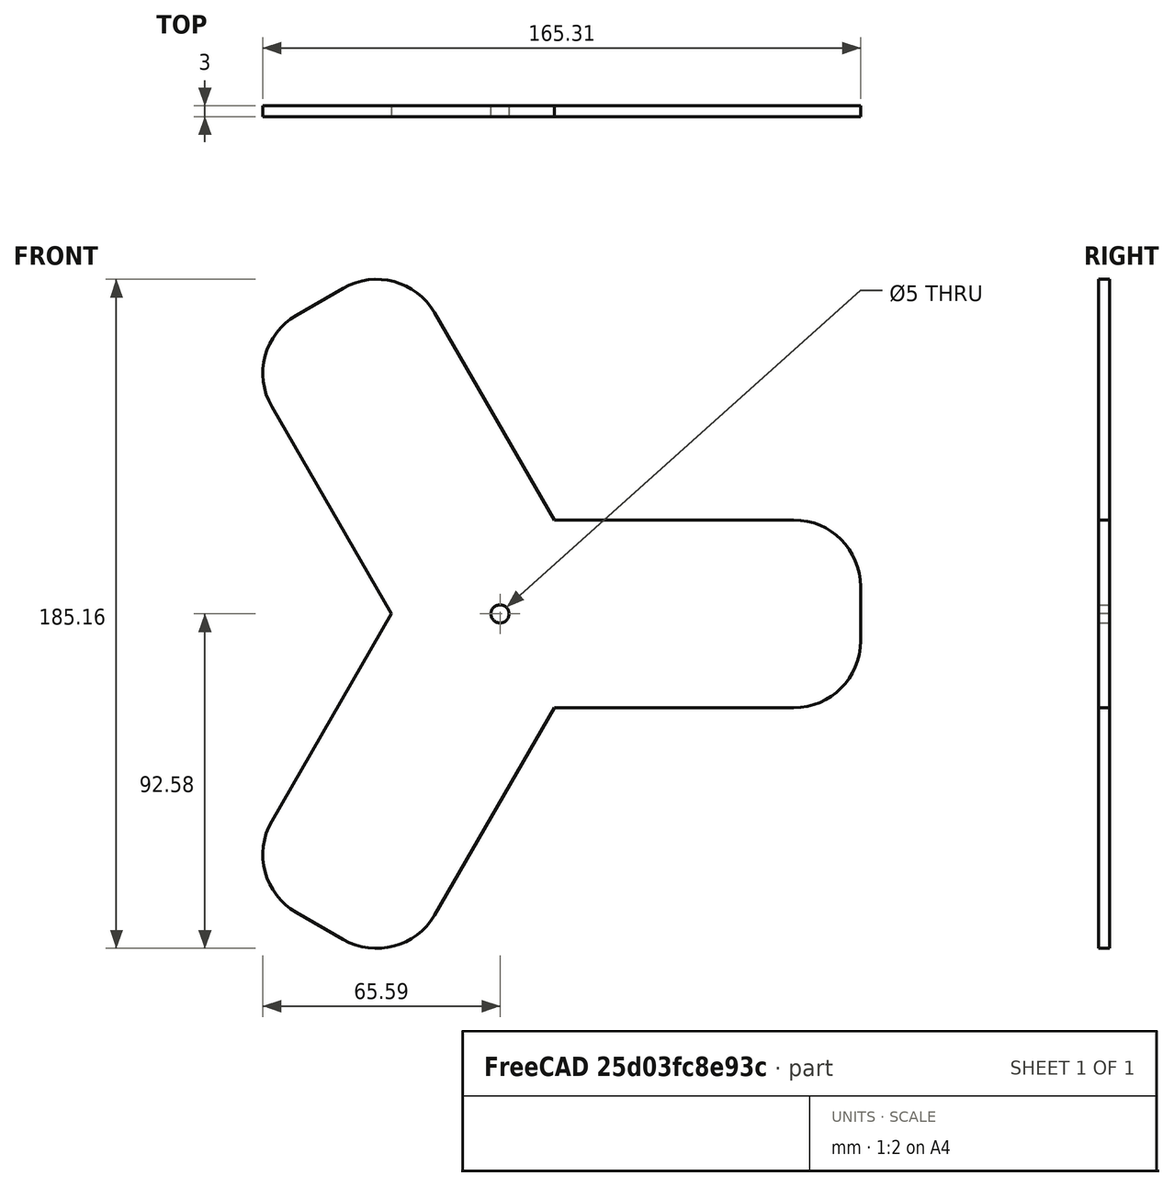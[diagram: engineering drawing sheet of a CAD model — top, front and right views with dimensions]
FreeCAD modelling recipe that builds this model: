
FCSTD DOCUMENT  (FreeCAD 0.21R33771 (Git))
Label: rotor
License: Public Domain
LicenseURL: https://en.wikipedia.org/wiki/Public_domain
objects: PartDesign::CoordinateSystem×1, Sketcher::SketchObject×1, Part::Extrusion×1, PartDesign::Line×1, App::Part×1
note: 4 computed .brp shape members not serialized (recipe doc carries the construction recipe); baked Part::Feature solids carry a one-line shape summary decoded from their .brp

FEATURE [PartDesign::CoordinateSystem] LCS_Origin
  AttacherType = Attacher::AttachEngine3D
  MapMode = 2
  Support = -> [X_Axis]
FEATURE [Sketcher::SketchObject] Sketch
  FullyConstrained = true
  Placement = pos=(0,0,0) rot=(1,0,0;1.5708rad)
  sketch-geometry (23):
    g0: Circle CenterX=-80 CenterY=0 CenterZ=0 NormalX=0 NormalY=0 NormalZ=1 AngleXU=0 Radius=5
    g1: Circle CenterX=80 CenterY=0 CenterZ=0 NormalX=0 NormalY=0 NormalZ=1 AngleXU=0 Radius=5
    g2: Circle CenterX=0 CenterY=0 CenterZ=0 NormalX=0 NormalY=0 NormalZ=1 AngleXU=0 Radius=100
    g3: LineSegment StartX=-30 StartY=3.6e-15 StartZ=0 EndX=15 EndY=-25.9808 EndZ=0
    g4: LineSegment StartX=15 StartY=-25.9808 StartZ=0 EndX=15 EndY=25.9808 EndZ=0
    g5: LineSegment StartX=15 StartY=25.9808 StartZ=0 EndX=-30 EndY=3.6e-15 EndZ=0
    g6: Circle CenterX=0 CenterY=0 CenterZ=0 NormalX=0 NormalY=0 NormalZ=1 AngleXU=0 Radius=30
    g7: LineSegment StartX=15 StartY=25.9808 StartZ=0 EndX=81.2376 EndY=25.9808 EndZ=0
    g8: LineSegment StartX=15 StartY=-25.9808 StartZ=0 EndX=81.2376 EndY=-25.9808 EndZ=0
    g9: LineSegment StartX=15 StartY=25.9808 StartZ=0 EndX=-18.1188 EndY=83.3442 EndZ=0
    g10: LineSegment StartX=-30 StartY=3.6e-15 StartZ=0 EndX=-63.1188 EndY=57.3634 EndZ=0
    g11: LineSegment StartX=-30 StartY=3.6e-15 StartZ=0 EndX=-63.1188 EndY=-57.3634 EndZ=0
    g12: LineSegment StartX=15 StartY=-25.9808 StartZ=0 EndX=-18.1188 EndY=-83.3442 EndZ=0
    g13: LineSegment StartX=-56.3544 StartY=-82.6086 StartZ=0 EndX=-43.3641 EndY=-90.1086 EndZ=0
    g14: LineSegment StartX=-56.3544 StartY=82.6086 StartZ=0 EndX=-43.364 EndY=90.1086 EndZ=0
    g15: LineSegment StartX=99.7184 StartY=7.5 StartZ=0 EndX=99.7184 EndY=-7.5 EndZ=0
    g16: Circle CenterX=0 CenterY=0 CenterZ=0 NormalX=0 NormalY=0 NormalZ=1 AngleXU=0 Radius=2.5
    g17: ArcOfCircle CenterX=-47.114 CenterY=66.6038 CenterZ=0 NormalX=0 NormalY=0 NormalZ=1 AngleXU=0 Radius=18.4808 StartAngle=2.0944 EndAngle=3.66519
    g18: ArcOfCircle CenterX=-34.1236 CenterY=74.1038 CenterZ=0 NormalX=0 NormalY=0 NormalZ=1 AngleXU=0 Radius=18.4808 StartAngle=0.523599 EndAngle=2.0944
    g19: ArcOfCircle CenterX=81.2376 CenterY=7.5 CenterZ=0 NormalX=0 NormalY=0 NormalZ=1 AngleXU=0 Radius=18.4808 StartAngle=-1.8e-15 EndAngle=1.5708
    g20: ArcOfCircle CenterX=81.2376 CenterY=-7.5 CenterZ=0 NormalX=0 NormalY=0 NormalZ=1 AngleXU=0 Radius=18.4808 StartAngle=4.71239 EndAngle=6.28319
    g21: ArcOfCircle CenterX=-34.1236 CenterY=-74.1039 CenterZ=0 NormalX=0 NormalY=0 NormalZ=1 AngleXU=0 Radius=18.4808 StartAngle=4.18879 EndAngle=5.75959
    g22: ArcOfCircle CenterX=-47.114 CenterY=-66.6038 CenterZ=0 NormalX=0 NormalY=0 NormalZ=1 AngleXU=0 Radius=18.4808 StartAngle=2.61799 EndAngle=4.18879
  constraints (56):
    c: PointOnObject(g1,g-1)
    c: Equal(g1,g0)
    c: Radius(g1) = 5
    c: Symmetric(g0,g1,g-1)
    c: DistanceX(g1) = 80
    c: Radius(g2) = 100
    c: Coincident(g3,g4)
    c: Coincident(g4,g5)
    c: Coincident(g5,g3)
    c: Equal(g3,g4)
    c: Equal(g3,g5)
    c: PointOnObject(g3,g6)
    c: PointOnObject(g4,g6)
    c: PointOnObject(g5,g6)
    c: Vertical(g4)
    c: Coincident(g7,g4)
    c: Horizontal(g7)
    c: Coincident(g8,g3)
    c: Horizontal(g8)
    c: Coincident(g9,g7)
    c: Coincident(g10,g3)
    c: Perpendicular(g5,g9)
    c: Perpendicular(g5,g10)
    c: Coincident(g11,g10)
    c: Coincident(g12,g8)
    c: Perpendicular(g3,g12)
    c: Perpendicular(g3,g11)
    c: Coincident(g6,g-1)
    c: Coincident(g2,g6)
    c: Coincident(g16,g2)
    c: Radius(g16) = 2.5
    c: Tangent(g10,g17) = 1.5708
    c: Tangent(g14,g17) = 1.5708
    c: Tangent(g14,g18) = 1.5708
    c: Tangent(g9,g18) = -1.5708
    c: Tangent(g7,g19) = 1.5708
    c: Tangent(g15,g19) = 1.5708
    c: Tangent(g15,g20) = 1.5708
    c: Tangent(g8,g20) = -1.5708
    c: Tangent(g12,g21) = 1.5708
    c: Tangent(g13,g21) = -1.5708
    c: Tangent(g11,g22) = -1.5708
    c: Tangent(g13,g22) = -1.5708
    c: Equal(g13,g14)
    c: Equal(g14,g15)
    c: Equal(g17,g18)
    c: Equal(g18,g19)
    c: Equal(g19,g20)
    c: Equal(g20,g21)
    c: Equal(g21,g22)
    c: PointOnObject(g15,g2)
    c: PointOnObject(g15,g2)
    c: PointOnObject(g14,g2)
    c: PointOnObject(g13,g2)
    c: DistanceY(g15,g15) = 15
    c: Radius(g6) = 30
FEATURE [Part::Extrusion] Extrude
  Base = -> Sketch
  Dir = (0,-1,-3e-16)
  DirMode = 2
  FaceMakerClass = Part::FaceMakerBullseye
  LengthFwd = 3
  LengthRev = 0
  Solid = true
  Symmetric = true
FEATURE [PartDesign::Line] HoleAxis_1  label="Axle AP"
  AttacherType = Attacher::AttachEngineLine
  AttachmentOffset = pos=(0,0,-1.5) rot=(0,0,1;-0.523599rad)
  Length = 7.04534
  MapMode = 19
  Placement = pos=(0,0,-7e-16) rot=(-0.935113,-0.250563,0.250563;4.64535rad)
  ResizeMode = 1
  Support = -> [Extrude]
FEATURE [App::Part] Rotor
  Group = -> [LCS_Origin,Sketch,Extrude,HoleAxis_1]
  Origin = -> Origin
